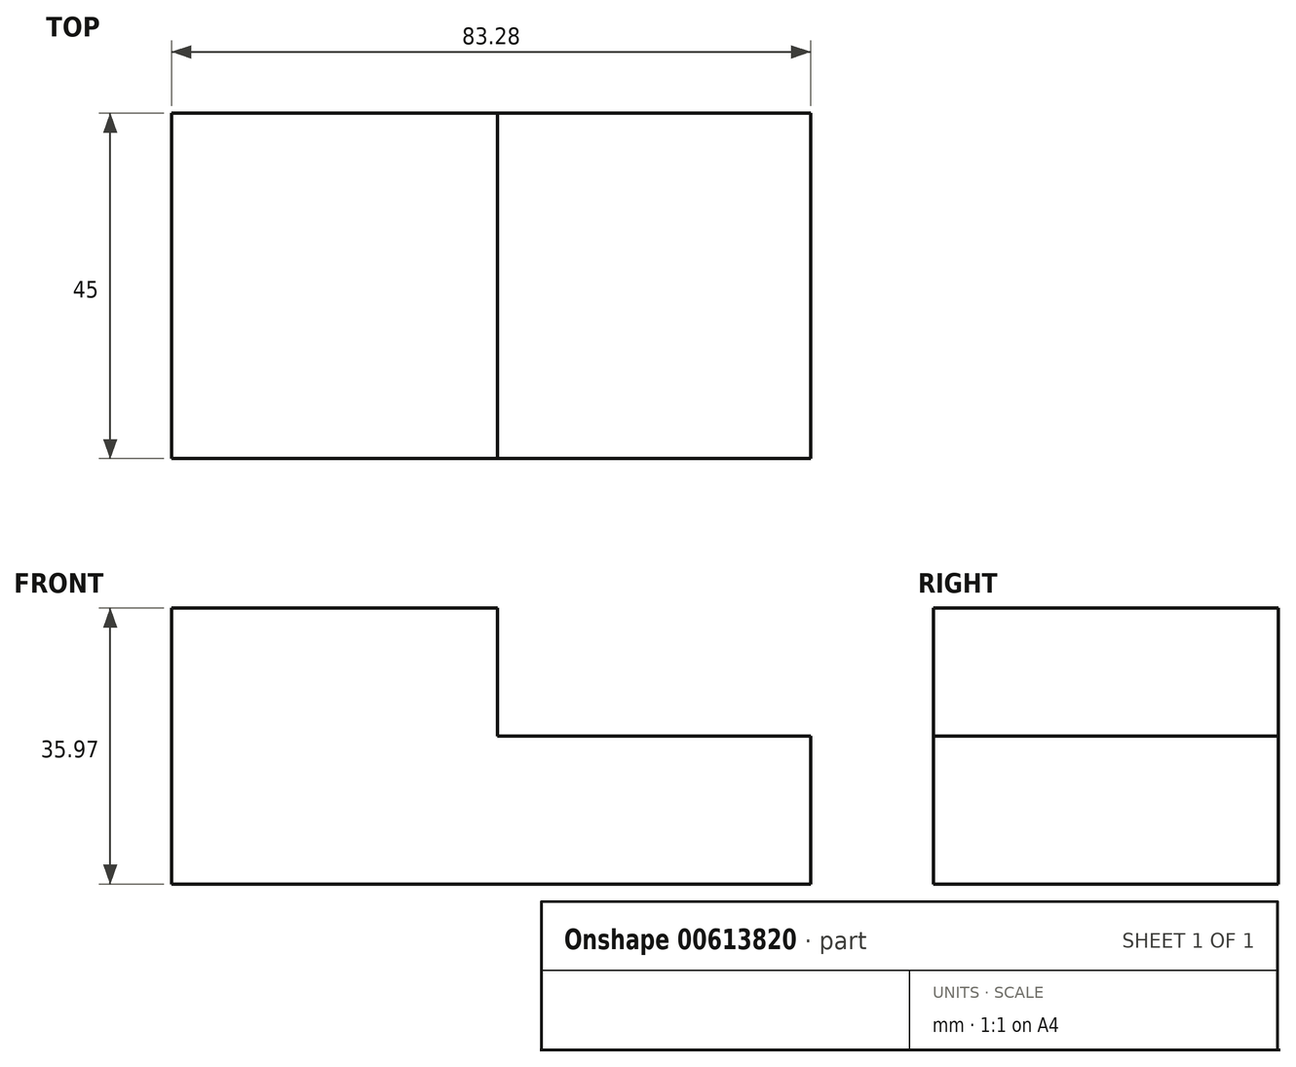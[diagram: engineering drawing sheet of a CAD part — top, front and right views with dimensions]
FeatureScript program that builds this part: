
annotation { "Feature Type Name" : "Feature", "Feature Type Description" : "" }
export const myFeature = defineFeature(function(context is Context, id is Id, definition is map)
    precondition{}
    {
        {
            var Q0;
            Q0=qCreatedBy(makeId("Front.planeOp"),FACE);
            var sketch = newSketch(context, id + "F0", { "sketchPlane" : qUnion([Q0])});
            skLineSegment(sketch, "E0", {"start": v(-49.15, 30.45) * mm, "end": v(-6.66, 30.45) * mm});
            skLineSegment(sketch, "E1", {"start": v(-6.66, 30.45) * mm, "end": v(-6.66, 13.74) * mm});
            skLineSegment(sketch, "E2", {"start": v(-6.66, 13.74) * mm, "end": v(34.13, 13.74) * mm});
            skLineSegment(sketch, "E3", {"start": v(34.13, 13.74) * mm, "end": v(34.13, -5.52) * mm});
            skLineSegment(sketch, "E4", {"start": v(34.13, -5.52) * mm, "end": v(-49.15, -5.52) * mm});
            skLineSegment(sketch, "E5", {"start": v(-49.15, -5.52) * mm, "end": v(-49.15, 30.45) * mm});
            skSolve(sketch);
        }
        {
            var Q0;
            Q0 = qSketchRegion(id + "F0", true);
            extrude(context, id + "F1", {"entities" : qUnion([Q0]), "depth" : 45 * mm, "offsetDistance" : 25 * mm});
        }
    });
